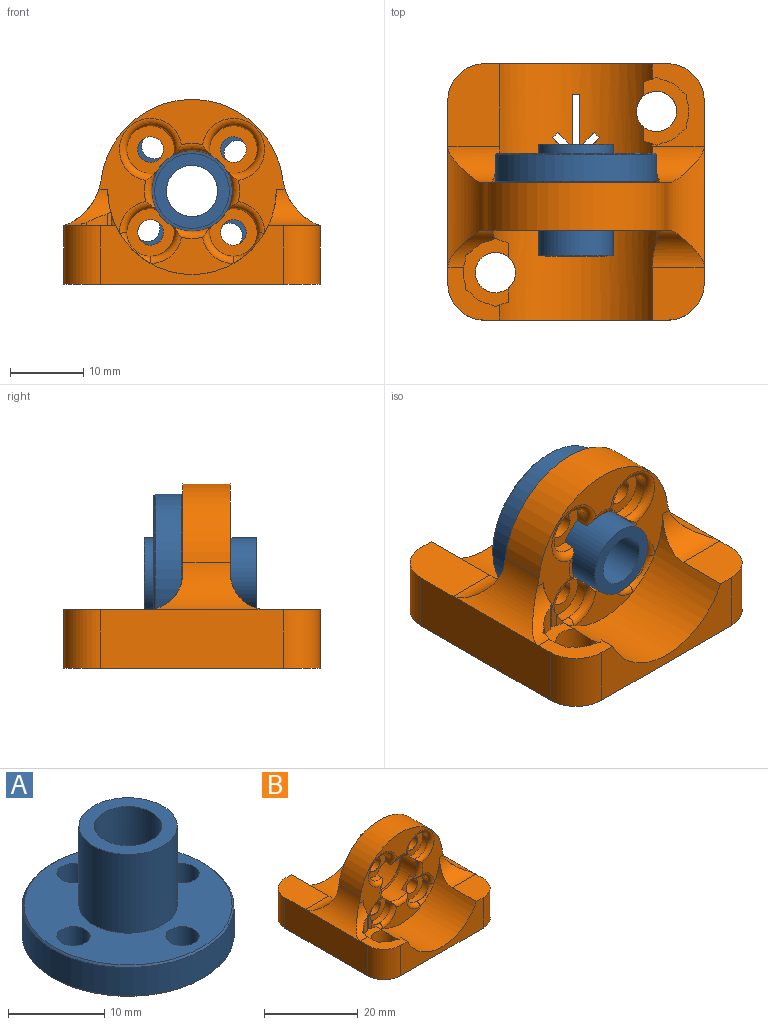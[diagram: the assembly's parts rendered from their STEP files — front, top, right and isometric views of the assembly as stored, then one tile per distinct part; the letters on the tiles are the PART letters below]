
ASSEMBLY  parts=2 mates=1
PART A: 14 faces, bbox 22x22x15.3 mm
  f0: plane 21.63x21.63mm, normal (0,0,-1), area 247.4mm2, adj f7,f8,f10,f11,f12,f13
  f1: plane 21.63x21.63mm, normal (0,0,1), area 248.2mm2, adj f5,f9,f10,f11,f12,f13
  f2: cylinder r=11.01mm len=22.03mm, axis (0,0,-1), area 249.1mm2, adj f8,f9
  f3: cylinder r=3.5mm len=15.25mm, axis (0,0,-1), area 335.4mm2, adj f4,f6
  f4: plane 10.2x10.2mm, normal (0,0,1), area 43.2mm2, adj f3,f5
  f5: cylinder r=5.1mm len=10.2mm, axis (0,0,-1), area 320.4mm2, adj f1,f4
  f6: plane 10.25x10.25mm, normal (0,0,-1), area 44mm2, adj f3,f7
  f7: cylinder r=5.12mm len=10.25mm, axis (0,0,1), area 40.3mm2, adj f0,f6
  f8: cone r=11.01mm half-angle=45deg, axis (0,0,1), area 19.4mm2, adj f0,f2
  f9: cone r=10.81mm half-angle=45deg, axis (0,0,-1), area 19.4mm2, adj f1,f2
  f10: cylinder r=1.72mm len=4mm, axis (0,0,1), area 43.4mm2, adj f0,f1
  f11: cylinder r=1.72mm len=4mm, axis (0,0,1), area 43.4mm2, adj f0,f1
  f12: cylinder r=1.72mm len=4mm, axis (0,0,1), area 43.4mm2, adj f0,f1
  f13: cylinder r=1.72mm len=4mm, axis (0,0,1), area 43.4mm2, adj f0,f1
PART B: 90 faces, bbox 35x35x25.3 mm
  f0: plane 11.33x5.07mm, normal (0,-1,0), area 28.9mm2, adj f19,f78,f80,f82
  f1: cylinder r=11.5mm len=23mm, axis (0,-1,0), area 396.1mm2, adj f15,f17,f20,f24,f27,f38,f45,f46
  f2: plane 35x35mm, normal (0,0,-1), area 1140.6mm2, adj f17,f18,f21,f22,f23,f24,f56,f57
  f3: cylinder r=5.5mm len=11mm, axis (0,1,0), area 134.8mm2, adj f60,f61,f62,f63,f64,f65,f66,f67
  f4: cylinder r=1.75mm len=4mm, axis (0,1,0), area 44mm2, adj f27,f61,f89
  f5: cylinder r=1.75mm len=4mm, axis (0,1,0), area 44mm2, adj f27,f67,f89
  f6: cylinder r=1.75mm len=4mm, axis (0,1,0), area 44mm2, adj f27,f63,f89
  f7: cylinder r=1.75mm len=4mm, axis (0,1,0), area 44mm2, adj f27,f65,f89
  f8: plane 25.43x18.24mm, normal (0,-1,0), area 121.2mm2, adj f19,f26,f28,f29,f52,f53,f79,f81
  f9: plane 3.88x0.61mm, normal (0.5,-0.87,0), area 2.6mm2, adj f19,f31,f32,f49,f52
  f10: plane 2.26x0.69mm, normal (1,0,0), area 1.5mm2, adj f32,f33,f48,f52
  f11: plane 2x0.6mm, normal (0.5,0.87,0), area 1.4mm2, adj f16,f32,f34,f47
  f12: plane 2x0.54mm, normal (-0.5,-0.87,0), area 1.2mm2, adj f15,f38,f41,f44
  f13: plane 2x0.54mm, normal (-0.5,0.87,0), area 1.2mm2, adj f15,f37,f38,f43
  f14: plane 2x0.62mm, normal (-1,0,0), area 1.2mm2, adj f15,f38,f40,f42
  f15: plane 11.25x7.07mm, normal (0,0,1), area 38.2mm2, adj f1,f12,f13,f14,f23,f24,f36,f37
  f16: plane 7.25x7.07mm, normal (0,0,1), area 24.1mm2, adj f11,f19,f21,f22,f30,f34,f35,f47
  f17: cylinder r=2.75mm len=6mm, axis (0,0,-1), area 99.9mm2, adj f1,f2,f38
  f18: cylinder r=2.75mm len=6mm, axis (0,0,-1), area 99.9mm2, adj f2,f19,f32
  f19: cylinder r=11.5mm len=23mm, axis (0,-1,0), area 304.8mm2, adj f0,f8,f9,f16,f18,f22,f25,f30
  f20: plane 11.25x7.07mm, normal (0,0,1), area 74.2mm2, adj f1,f21,f24,f54,f59
  f21: plane 25x8mm, normal (-1,0,0), area 200mm2, adj f2,f16,f20,f28,f56,f59
  f22: plane 25x8mm, normal (0,-1,0), area 100.4mm2, adj f2,f16,f19,f25,f56,f57
  f23: plane 25x8mm, normal (1,0,0), area 200mm2, adj f2,f15,f25,f29,f57,f58
  f24: plane 25x8mm, normal (0,1,0), area 100.4mm2, adj f1,f2,f15,f20,f58,f59
  f25: plane 7.25x7.07mm, normal (0,0,1), area 45.9mm2, adj f19,f22,f23,f53,f57
  f26: cylinder r=12.5mm len=24.78mm, axis (0,1,0), area 233.5mm2, adj f8,f27,f28,f29
  f27: plane 25.43x23.9mm, normal (0,1,0), area 280.5mm2, adj f1,f4,f5,f6,f7,f26,f28,f29
  f28: cylinder r=8mm len=16.5mm, axis (0,-1,0), area 75.9mm2, adj f8,f21,f26,f27,f52,f54
  f29: cylinder r=8mm len=16.5mm, axis (0,-1,0), area 75.9mm2, adj f8,f23,f26,f27,f53,f55
  f30: plane 2x0.6mm, normal (-0.5,0.87,0), area 1.4mm2, adj f16,f19,f32,f35,f51
  f31: plane 3.53x0.63mm, normal (-0.5,-0.87,0), area 1.8mm2, adj f9,f19,f32,f50
  f32: plane 9.41x6.16mm, normal (0,0,1), area 25.3mm2, adj f9,f10,f11,f18,f19,f30,f31,f33
  f33: plane 2.4x0.6mm, normal (0.5,-0.87,0), area 1.6mm2, adj f10,f32,f49,f52
  f34: plane 2x0.69mm, normal (1,0,0), area 1.4mm2, adj f11,f16,f32,f48
  f35: plane 2x0.6mm, normal (0.5,0.87,0), area 1.4mm2, adj f16,f30,f32,f47
  f36: plane 2x0.54mm, normal (0.5,-0.87,0), area 1.2mm2, adj f15,f38,f39,f46
  f37: plane 2x0.54mm, normal (0.5,0.87,0), area 1.2mm2, adj f13,f15,f38,f45
  f38: plane 9.35x6.16mm, normal (0,0,1), area 25.2mm2, adj f1,f12,f13,f14,f17,f36,f37,f39
  f39: plane 2x0.54mm, normal (-0.5,-0.87,0), area 1.2mm2, adj f15,f36,f38,f44
  f40: plane 2x0.54mm, normal (-0.5,0.87,0), area 1.2mm2, adj f14,f15,f38,f43
  f41: plane 2x0.62mm, normal (-1,0,0), area 1.2mm2, adj f12,f15,f38,f42
  f42: cylinder r=4.4mm len=3.44mm, axis (0,0,1), area 7.1mm2, adj f14,f15,f38,f41
  f43: cylinder r=4.4mm len=2.98mm, axis (0,0,1), area 7.1mm2, adj f13,f15,f38,f40
  f44: cylinder r=4.4mm len=2.98mm, axis (0,0,1), area 7.1mm2, adj f12,f15,f38,f39
  f45: cylinder r=4.4mm len=2mm, axis (0,0,1), area 1.2mm2, adj f1,f15,f37,f38
  f46: cylinder r=4.4mm len=2mm, axis (0,0,1), area 1.2mm2, adj f1,f15,f36,f38
  f47: cylinder r=4.4mm len=2.87mm, axis (0,0,1), area 6.8mm2, adj f11,f16,f32,f35
  f48: cylinder r=4.4mm len=3.32mm, axis (0,0,1), area 6.8mm2, adj f10,f16,f32,f34,f52
  f49: cylinder r=4.4mm len=3.54mm, axis (0,0,1), area 10.1mm2, adj f9,f32,f33,f52
  f50: cylinder r=4.4mm len=1.94mm, axis (0,0,1), area 1.2mm2, adj f19,f31,f32
  f51: cylinder r=4.4mm len=1.94mm, axis (0,0,1), area 1.2mm2, adj f19,f30,f32
  f52: cylinder r=5mm len=6.39mm, axis (-1,0,0), area 18.1mm2, adj f8,f9,f10,f16,f19,f28,f33,f48
  f53: cylinder r=5mm len=7.07mm, axis (-1,0,0), area 32.7mm2, adj f8,f19,f25,f29
  f54: cylinder r=5mm len=7.07mm, axis (1,0,0), area 32.7mm2, adj f1,f20,f27,f28
  f55: cylinder r=5mm len=7.07mm, axis (1,0,0), area 32.7mm2, adj f1,f15,f27,f29
  f56: cylinder r=5mm len=8mm, axis (0,0,-1), area 62.8mm2, adj f2,f16,f21,f22
  f57: cylinder r=5mm len=8mm, axis (0,0,1), area 62.8mm2, adj f2,f22,f23,f25
  f58: cylinder r=5mm len=8mm, axis (0,0,-1), area 62.8mm2, adj f2,f15,f23,f24
  f59: cylinder r=5mm len=8mm, axis (0,0,1), area 62.8mm2, adj f2,f20,f21,f24
  f60: cylinder r=3.25mm len=6.5mm, axis (0,-1,0), area 25.3mm2, adj f3,f61,f83
  f61: plane 6.5x6.5mm, normal (0,-1,0), area 21.8mm2, adj f3,f4,f60
  f62: cylinder r=3.25mm len=6.5mm, axis (0,-1,0), area 26.3mm2, adj f3,f63,f82,f84,f86
  f63: plane 6.5x6.5mm, normal (0,-1,0), area 21.8mm2, adj f3,f6,f62
  f64: cylinder r=3.25mm len=6.5mm, axis (0,-1,0), area 25.3mm2, adj f3,f65,f87
  f65: plane 6.5x6.5mm, normal (0,-1,0), area 21.8mm2, adj f3,f7,f64
  f66: cylinder r=3.25mm len=6.5mm, axis (0,-1,0), area 26.3mm2, adj f3,f67,f77,f78,f79
  f67: plane 6.5x6.5mm, normal (0,-1,0), area 21.8mm2, adj f3,f5,f66
  f68: plane 1.8x0.71mm, normal (-0.71,-0.71,0), area 1.7mm2, adj f1,f2,f69,f76
  f69: plane 3.21x3.21mm, normal (-0.71,0.71,0), area 6.7mm2, adj f1,f2,f68,f70
  f70: plane 3.21x3.21mm, normal (0.71,0.71,0), area 6.7mm2, adj f1,f2,f69,f71
  f71: plane 1.8x0.71mm, normal (0.71,-0.71,0), area 1.7mm2, adj f1,f2,f70,f72
  f72: plane 1.99x1.99mm, normal (-0.71,-0.71,0), area 4.1mm2, adj f1,f2,f71,f73
  f73: plane 7.19x1.36mm, normal (1,0,0), area 9.8mm2, adj f1,f2,f72,f74
  f74: plane 1.36x1mm, normal (0,-1,0), area 1.4mm2, adj f1,f2,f73,f75
  f75: plane 7.19x1.36mm, normal (-1,0,0), area 9.8mm2, adj f1,f2,f74,f76
  f76: plane 1.99x1.99mm, normal (0.71,-0.71,0), area 4.1mm2, adj f1,f2,f68,f75
  f77: bspline ~4.68x4.5mm, area 5.1mm2, adj f19,f66,f78,f79
  f78: torus R=4.25mm, axis (0,-1,0), area 9.1mm2, adj f0,f66,f77,f80
  f79: torus R=4.25mm, axis (0,-1,0), area 9.2mm2, adj f8,f66,f77,f81
  f80: torus R=6.5mm, axis (0,-1,0), area 6.4mm2, adj f0,f3,f78,f82
  f81: torus R=6.5mm, axis (0,-1,0), area 6.4mm2, adj f3,f8,f79,f83
  f82: torus R=4.25mm, axis (0,-1,0), area 9.1mm2, adj f0,f62,f80,f84
  f83: torus R=4.25mm, axis (0,-1,0), area 27.1mm2, adj f8,f60,f81,f85
  f84: bspline ~4.24x4.19mm, area 5.1mm2, adj f19,f62,f82,f86
  f85: torus R=6.5mm, axis (0,-1,0), area 6.4mm2, adj f3,f8,f83,f87
  f86: torus R=4.25mm, axis (0,-1,0), area 9.2mm2, adj f8,f62,f84,f88
  f87: torus R=4.25mm, axis (0,-1,0), area 27.1mm2, adj f8,f64,f85,f88
  f88: torus R=6.5mm, axis (0,-1,0), area 6.4mm2, adj f3,f8,f86,f87
  f89: torus R=6.5mm, axis (0,-1,0), area 56.8mm2, adj f3,f4,f5,f6,f7,f27
PLACE A rot(axis=(0.89,-0.32,0.32),96.8deg) t=(0,5.25,12.75)mm
PLACE B at identity fixed
MATE planar B.f27 <-> A.f2  axis (0,1,0) through (0,1.25,13.85)mm
